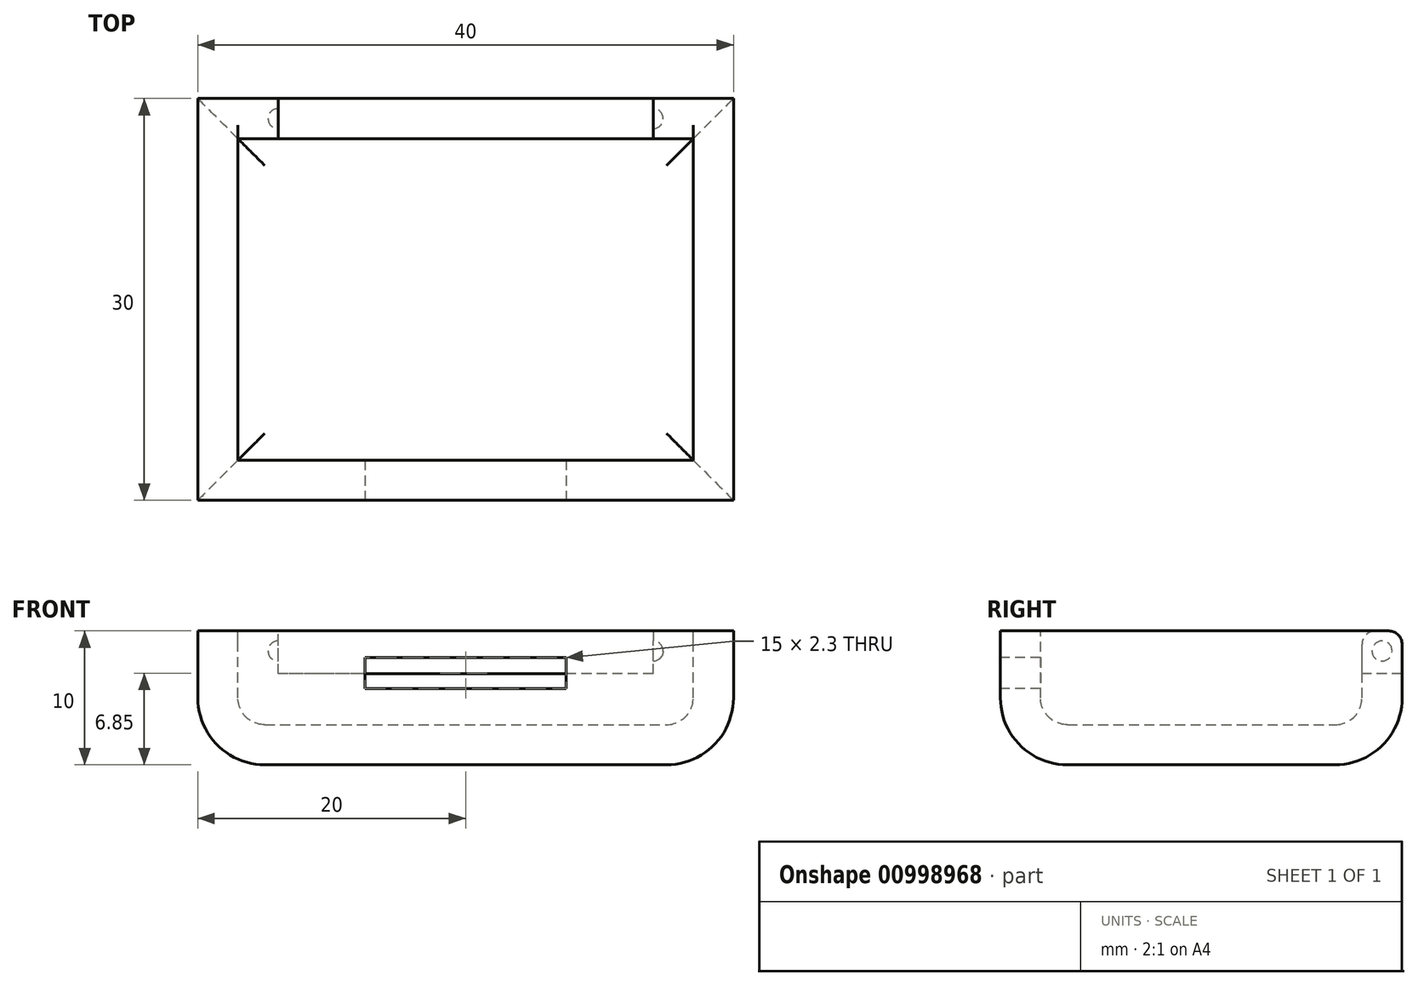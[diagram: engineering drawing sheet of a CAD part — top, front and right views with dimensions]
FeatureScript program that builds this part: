
annotation { "Feature Type Name" : "Feature", "Feature Type Description" : "" }
export const myFeature = defineFeature(function(context is Context, id is Id, definition is map)
    precondition{}
    {
        {
            var Q0;
            Q0=qCreatedBy(makeId("Top.planeOp"),FACE);
            var sketch = newSketch(context, id + "F0", { "sketchPlane" : qUnion([Q0])});
            skLineSegment(sketch, "E0.bottom", {"start": v(20, 15) * mm, "end": v(-20, 15) * mm});
            skLineSegment(sketch, "E0.top", {"start": v(20, -15) * mm, "end": v(-20, -15) * mm});
            skLineSegment(sketch, "E0.left", {"start": v(20, 15) * mm, "end": v(20, -15) * mm});
            skLineSegment(sketch, "E0.right", {"start": v(-20, 15) * mm, "end": v(-20, -15) * mm});
            skPoint(sketch, "E0.middle", {"position": v(0, 0) * mm});
            skSolve(sketch);
        }
        {
            var Q0;
            Q0=qSketchRegion(id+"F0",true);
            extrude(context, id + "F1", {"entities" : qUnion([Q0]), "oppositeDirection" : true, "depth" : 10 * mm, "offsetDistance" : 25 * mm});
        }
        {
            var Q0;
            Q0=makeQuery(id+"F1.opExtrude","CAP_FACE",FACE,{"disambiguationData":[OSD([sQuery(id+"F0.wireOp",EDGE,"E0.bottom"),sQuery(id+"F0.wireOp",EDGE,"E0.top"),sQuery(id+"F0.wireOp",EDGE,"E0.left"),sQuery(id+"F0.wireOp",EDGE,"E0.right")])],"isStart":false});
            fillet(context, id + "F2", {"entities" : qUnion([Q0]), "radius" : 5 * mm, "tangentPropagation" : true, "allowEdgeOverflow" : false});
        }
        {
            var Q0;
            Q0=makeQuery(id+"F1.opExtrude","CAP_FACE",FACE,{"disambiguationData":[OSD([sQuery(id+"F0.wireOp",EDGE,"E0.bottom"),sQuery(id+"F0.wireOp",EDGE,"E0.top"),sQuery(id+"F0.wireOp",EDGE,"E0.left"),sQuery(id+"F0.wireOp",EDGE,"E0.right")])],"isStart":true});
            shell(context, id + "F3", {"entities" : qUnion([Q0]), "thickness" : 3 * mm});
        }
        {
            var Q0;
            Q0=makeQuery(id+"F1.opExtrude","CAP_FACE",FACE,{"disambiguationData":[OSD([sQuery(id+"F0.wireOp",EDGE,"E0.bottom"),sQuery(id+"F0.wireOp",EDGE,"E0.top"),sQuery(id+"F0.wireOp",EDGE,"E0.left"),sQuery(id+"F0.wireOp",EDGE,"E0.right")])],"isStart":true});
            var sketch = newSketch(context, id + "F4", { "sketchPlane" : qUnion([Q0])});
            skLineSegment(sketch, "E1.bottom", {"start": v(-14, 15) * mm, "end": v(14, 15) * mm});
            skLineSegment(sketch, "E1.top", {"start": v(-14, 12) * mm, "end": v(14, 12) * mm});
            skLineSegment(sketch, "E1.left", {"start": v(-14, 15) * mm, "end": v(-14, 12) * mm});
            skLineSegment(sketch, "E1.right", {"start": v(14, 15) * mm, "end": v(14, 12) * mm});
            skPoint(sketch, "E2", {"position": v(0, 15) * mm});
            skSolve(sketch);
        }
        {
            var Q0;
            Q0=qSketchRegion(id+"F4",true);
            extrude(context, id + "F5", {"entities" : qUnion([Q0]), "operationType" : NewBodyOperationType.REMOVE, "oppositeDirection" : true, "depth" : 3 * mm, "offsetDistance" : 25 * mm});
        }
        {
            var Q0;
            Q0=qCreatedBy(makeId("Top.planeOp"),FACE);
            var sketch = newSketch(context, id + "F6", { "sketchPlane" : qUnion([Q0])});
            skLineSegment(sketch, "E3.bottom", {"start": v(0, 28.07) * mm, "end": v(32.36, 28.07) * mm});
            skLineSegment(sketch, "E3.top", {"start": v(0, -32.18) * mm, "end": v(32.36, -32.18) * mm});
            skLineSegment(sketch, "E3.left", {"start": v(0, 28.07) * mm, "end": v(0, -32.18) * mm});
            skLineSegment(sketch, "E3.right", {"start": v(32.36, 28.07) * mm, "end": v(32.36, -32.18) * mm});
            skSolve(sketch);
        }
        {
            var Q0;
            Q0=qSketchRegion(id+"F6",true);
            extrude(context, id + "F7", {"entities" : qUnion([Q0]), "operationType" : NewBodyOperationType.REMOVE, "oppositeDirection" : true, "depth" : 25 * mm, "offsetDistance" : 25 * mm});
        }
        {
            var Q0;
            Q0=makeQuery(id+"F5.boolean.opBoolean","COPY",FACE,{"derivedFrom":makeQuery(id+"F5.opExtrude","SWEPT_FACE",FACE,{"disambiguationData":[OSD([sQuery(id+"F4.wireOp",EDGE,"E1.left")])]})});
            var sketch = newSketch(context, id + "F8", { "sketchPlane" : qUnion([Q0])});
            skCircle(sketch, "E4", {"center": v(13.5, -1.5) * mm, "radius": 0.75 * mm});
            skPoint(sketch, "E5", {"position": v(13.5, 0) * mm});
            skPoint(sketch, "E6", {"position": v(15, -1.5) * mm});
            skSolve(sketch);
        }
        {
            var Q0;
            Q0=makeQuery(id+"F8.imprint","IMPRINT",FACE,{"disambiguationData":[TD([[makeQuery(id+"F8.imprint","IMPRINT",EDGE,{"derivedFrom":sQuery(id+"F8.wireOp",EDGE,"E4")}),1.0]])]});
            var Q1;
            Q1=sQuery(id+"F8.wireOp",EDGE,"E4");
            extrude(context, id + "F9", {"entities" : qUnion([Q0]), "operationType" : NewBodyOperationType.REMOVE, "surfaceEntities" : qUnion([Q1]), "oppositeDirection" : true, "depth" : .75 * mm, "offsetDistance" : 25 * mm});
        }
        {
            var Q0;
            Q0=makeQuery(id+"F9.boolean.opBoolean","COPY",EDGE,{"derivedFrom":makeQuery(id+"F9.opExtrude","CAP_EDGE",EDGE,{"disambiguationData":[OSD([sQuery(id+"F8.wireOp",EDGE,"E4")])],"isStart":false})});
            fillet(context, id + "F10", {"entities" : qUnion([Q0]), "radius" : .75 * mm, "tangentPropagation" : true, "allowEdgeOverflow" : false});
        }
        {
            var Q0;
            Q0=makeQuery(id+"F5.boolean.opBoolean","COPY",FACE,{"derivedFrom":makeQuery(id+"F5.opExtrude","CAP_FACE",FACE,{"disambiguationData":[OSD([sQuery(id+"F4.wireOp",EDGE,"E1.bottom"),sQuery(id+"F4.wireOp",EDGE,"E1.top"),sQuery(id+"F4.wireOp",EDGE,"E1.left"),sQuery(id+"F4.wireOp",EDGE,"E1.right")])],"isStart":false})});
            var sketch = newSketch(context, id + "F11", { "sketchPlane" : qUnion([Q0])});
            skLineSegment(sketch, "E7.0.0", {"start": v(0, 12) * mm, "end": v(0, 15) * mm});
            skLineSegment(sketch, "E7.0.1", {"start": v(0, 15) * mm, "end": v(-14, 15) * mm});
            skLineSegment(sketch, "E7.0.2", {"start": v(-14, 15) * mm, "end": v(-14, 12) * mm});
            skLineSegment(sketch, "E7.0.3", {"start": v(-14, 12) * mm, "end": v(0, 12) * mm});
            skSolve(sketch);
        }
        {
            var Q0;
            Q0=qSketchRegion(id+"F11",true);
            extrude(context, id + "F12", {"entities" : qUnion([Q0]), "operationType" : NewBodyOperationType.REMOVE, "oppositeDirection" : true, "depth" : .2 * mm, "offsetDistance" : 25 * mm});
        }
        {
            var Q0;
            {var subQ0=sQuery(id+"F0.wireOp",EDGE,"E0.bottom");var subQ1=sQuery(id+"F0.wireOp",EDGE,"E0.right");Q0=makeQuery(id+"F5.boolean.opBoolean","SPLIT",EDGE,{"disambiguationData":[TD([makeQuery(id+"F1.opExtrude","SWEPT_FACE",FACE,{"disambiguationData":[OSD([subQ1])]})])],"derivedFrom":makeQuery(id+"F1.opExtrude","CAP_EDGE",EDGE,{"disambiguationData":[OSD([subQ0])],"isStart":true})});}
            var Q1;
            {var subQ1=sQuery(id+"F0.wireOp",EDGE,"E0.bottom");Q1=makeQuery(id+"F5.boolean.opBoolean","SPLIT",EDGE,{"disambiguationData":[TD([makeQuery(id+"F5.opExtrude","SWEPT_FACE",FACE,{"disambiguationData":[OSD([sQuery(id+"F4.wireOp",EDGE,"E1.left")])]})])],"derivedFrom":makeQuery(id+"F3.opShell","OFFSET_EDGE",EDGE,{"disambiguationData":[OSD([subQ1]),TDD([makeQuery(id+"F1.opExtrude","CAP_EDGE",EDGE,{"disambiguationData":[OSD([subQ1])],"isStart":true})])]})});}
            var Q2;
            Q2=makeQuery(id+"F12.boolean.opBoolean","COPY",EDGE,{"derivedFrom":makeQuery(id+"F12.opExtrude","CAP_EDGE",EDGE,{"disambiguationData":[OSD([sQuery(id+"F11.wireOp",EDGE,"E7.0.1")])],"isStart":false})});
            var Q3;
            Q3=makeQuery(id+"F12.boolean.opBoolean","COPY",EDGE,{"derivedFrom":makeQuery(id+"F12.opExtrude","CAP_EDGE",EDGE,{"disambiguationData":[OSD([sQuery(id+"F11.wireOp",EDGE,"E7.0.3")])],"isStart":false})});
            fillet(context, id + "F13", {"entities" : qUnion([Q0, Q1, Q2, Q3]), "radius" : 1 * mm, "tangentPropagation" : true, "allowEdgeOverflow" : false});
        }
        {
            var Q0;
            Q0=makeQuery(id+"F1.opExtrude","SWEPT_BODY",BODY,{"disambiguationData":[OSD([sQuery(id+"F0.wireOp",EDGE,"E0.bottom"),sQuery(id+"F0.wireOp",EDGE,"E0.top"),sQuery(id+"F0.wireOp",EDGE,"E0.left"),sQuery(id+"F0.wireOp",EDGE,"E0.right")])]});
            var Q1;
            Q1=qCreatedBy(makeId("Right.planeOp"),FACE);
            mirror(context, id + "F14", {"operationType" : NewBodyOperationType.ADD, "entities" : qUnion([Q0]), "mirrorPlane" : qUnion([Q1])});
        }
        {
            var Q0;
            {var subQ0=makeQuery(id+"F1.opExtrude","SWEPT_FACE",FACE,{"disambiguationData":[OSD([sQuery(id+"F0.wireOp",EDGE,"E0.top")])]});Q0=makeQuery(id+"F14.boolean.opBoolean","MERGE",FACE,{"derivedFrom":[subQ0,makeQuery(id+"F14.opPattern","COPY",FACE,{"derivedFrom":subQ0,"instanceName":"1"})]});}
            var sketch = newSketch(context, id + "F15", { "sketchPlane" : qUnion([Q0])});
            skLineSegment(sketch, "E8.bottom", {"start": v(7.5, -2) * mm, "end": v(-7.5, -2) * mm});
            skLineSegment(sketch, "E8.top", {"start": v(7.5, -4.3) * mm, "end": v(-7.5, -4.3) * mm});
            skLineSegment(sketch, "E8.left", {"start": v(7.5, -2) * mm, "end": v(7.5, -4.3) * mm});
            skLineSegment(sketch, "E8.right", {"start": v(-7.5, -2) * mm, "end": v(-7.5, -4.3) * mm});
            skPoint(sketch, "E8.middle", {"position": v(0, -3.15) * mm});
            skSolve(sketch);
        }
        {
            var Q0;
            Q0=qSketchRegion(id+"F15",true);
            extrude(context, id + "F16", {"entities" : qUnion([Q0]), "operationType" : NewBodyOperationType.REMOVE, "endBound" : BoundingType.UP_TO_NEXT, "oppositeDirection" : true, "depth" : 25 * mm, "offsetDistance" : 25 * mm});
        }
    });
